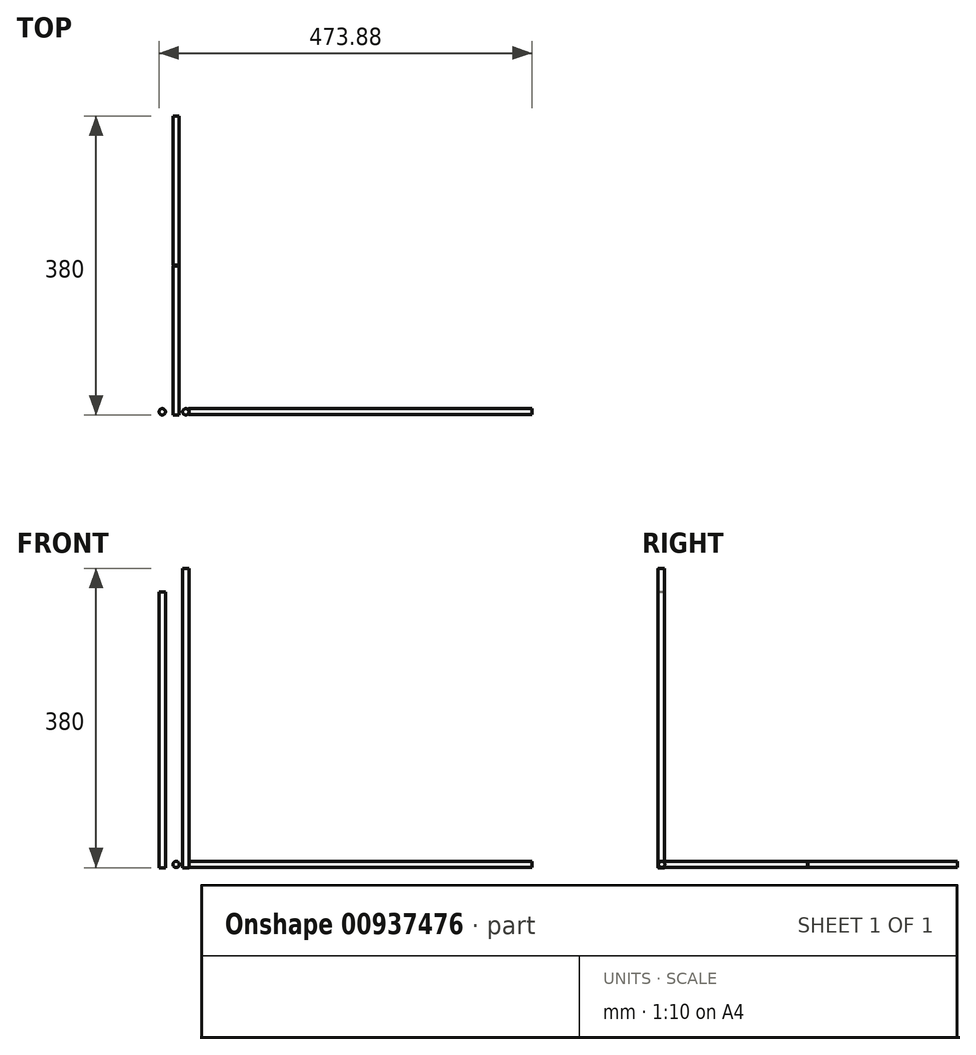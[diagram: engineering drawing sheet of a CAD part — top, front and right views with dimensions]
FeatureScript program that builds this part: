
annotation { "Feature Type Name" : "Feature", "Feature Type Description" : "" }
export const myFeature = defineFeature(function(context is Context, id is Id, definition is map)
    precondition{}
    {
        {
            var Q0;
            Q0=qCreatedBy(makeId("Top.planeOp"),FACE);
            var sketch = newSketch(context, id + "F0", { "sketchPlane" : qUnion([Q0])});
            skCircle(sketch, "E0", {"center": v(-4, 4.03) * mm, "radius": 4 * mm});
            skCircle(sketch, "E1", {"center": v(-33.88, 4.03) * mm, "radius": 4 * mm});
            skSolve(sketch);
        }
        {
            var Q0;
            Q0=makeQuery(id+"F0.imprint","IMPRINT",FACE,{"disambiguationData":[TD([[makeQuery(id+"F0.imprint","IMPRINT",EDGE,{"derivedFrom":sQuery(id+"F0.wireOp",EDGE,"E0")}),1.0]])]});
            extrude(context, id + "F1", {"entities" : qUnion([Q0]), "depth" : 380 * mm, "offsetDistance" : 25 * mm});
        }
        {
            var Q0;
            Q0=qCreatedBy(makeId("Front.planeOp"),FACE);
            var sketch = newSketch(context, id + "F2", { "sketchPlane" : qUnion([Q0])});
            skCircle(sketch, "E2", {"center": v(-16.24, 4.03) * mm, "radius": 4 * mm});
            skSolve(sketch);
        }
        {
            var Q0;
            Q0=qSketchRegion(id+"F2",true);
            extrude(context, id + "F3", {"entities" : qUnion([Q0]), "oppositeDirection" : true, "depth" : 380 * mm, "offsetDistance" : 25 * mm});
        }
        {
            var Q0;
            Q0=qCreatedBy(makeId("Right.planeOp"),FACE);
            var sketch = newSketch(context, id + "F4", { "sketchPlane" : qUnion([Q0])});
            skCircle(sketch, "E3", {"center": v(4.57, 4.13) * mm, "radius": 4 * mm});
            skSolve(sketch);
        }
        {
            var Q0;
            Q0=qSketchRegion(id+"F4",true);
            extrude(context, id + "F5", {"entities" : qUnion([Q0]), "depth" : 436 * mm, "offsetDistance" : 25 * mm});
        }
        {
            var Q0;
            Q0=makeQuery(id+"F0.imprint","IMPRINT",FACE,{"disambiguationData":[TD([[makeQuery(id+"F0.imprint","IMPRINT",EDGE,{"derivedFrom":sQuery(id+"F0.wireOp",EDGE,"E1")}),1.0]])]});
            extrude(context, id + "F6", {"entities" : qUnion([Q0]), "depth" : 350 * mm, "offsetDistance" : 25 * mm});
        }
        {
            var Q0;
            Q0=qCreatedBy(makeId("Front.planeOp"),FACE);
            cPlane(context, id + "F7", {"entities" : qUnion([Q0]), "cplaneType" : CPlaneType.OFFSET, "offset" : 190 * mm, "oppositeDirection" : true, "width" : 150 * mm, "height" : 150 * mm});
        }
        {
            var Q0;
            Q0=qCreatedBy(id+"F7.planeOp",FACE);
            var sketch = newSketch(context, id + "F8", { "sketchPlane" : qUnion([Q0])});
            skCircle(sketch, "E4.0", {"center": v(-16.24, 4.03) * mm, "radius": 4 * mm});
            skCircle(sketch, "E5", {"center": v(-16.24, 4.03) * mm, "radius": 3.45 * mm});
            skSolve(sketch);
        }
        {
            var Q0;
            Q0=qSketchRegion(id+"F8",true);
            extrude(context, id + "F9", {"entities" : qUnion([Q0]), "operationType" : NewBodyOperationType.REMOVE, "oppositeDirection" : true, "depth" : 1 * mm, "offsetDistance" : 25 * mm, "symmetric" : true});
        }
    });
